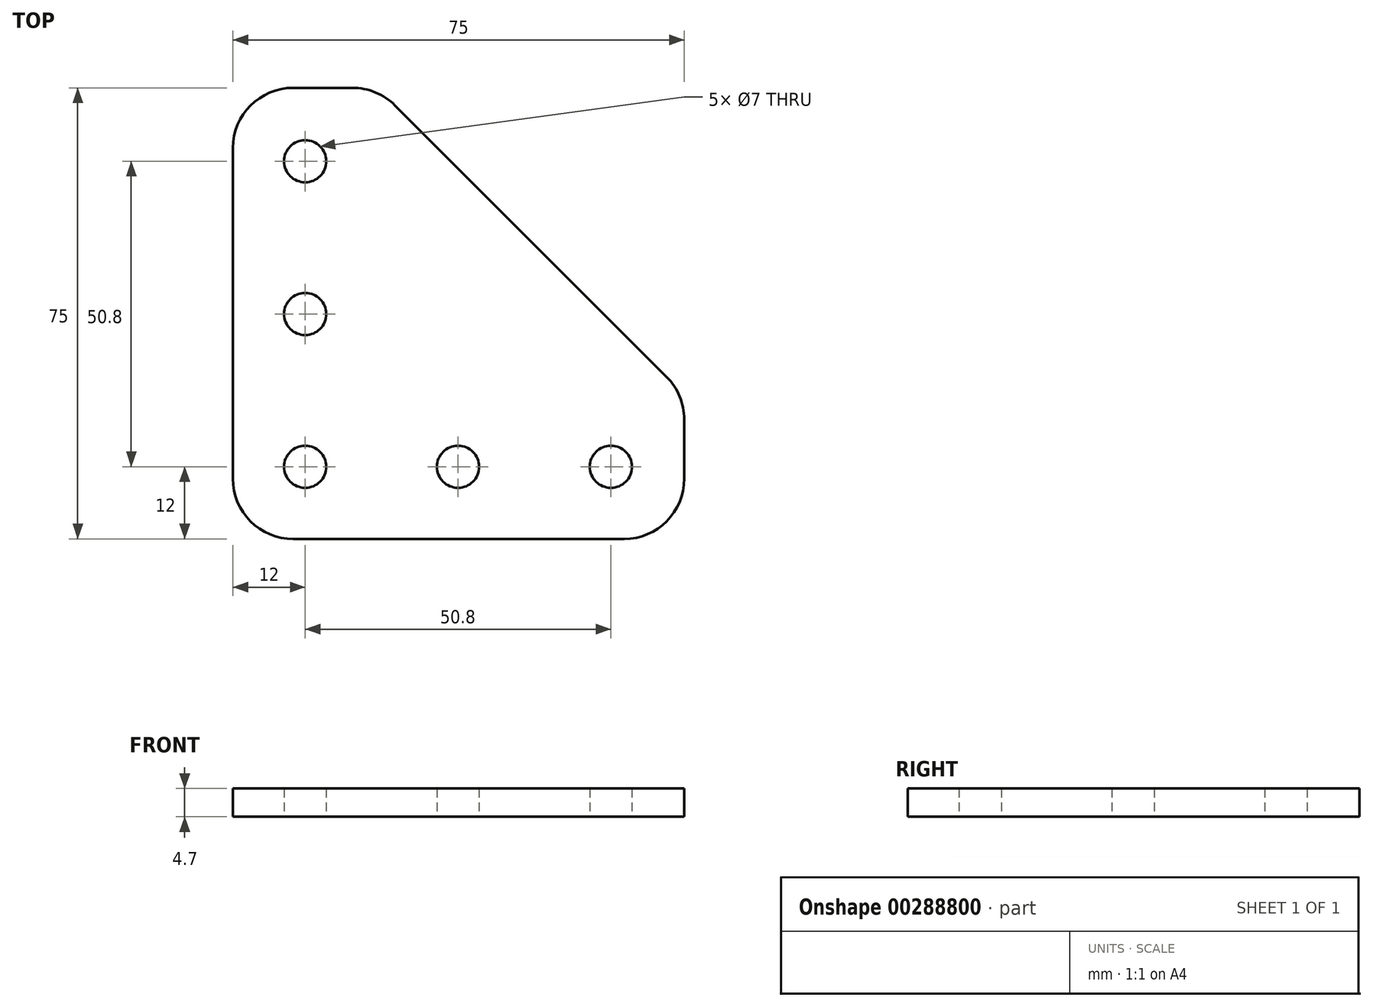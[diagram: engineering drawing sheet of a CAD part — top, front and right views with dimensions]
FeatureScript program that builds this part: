
annotation { "Feature Type Name" : "Feature", "Feature Type Description" : "" }
export const myFeature = defineFeature(function(context is Context, id is Id, definition is map)
    precondition{}
    {
        {
            var Q0;
            Q0=qCreatedBy(makeId("Top.planeOp"),FACE);
            var sketch = newSketch(context, id + "F0", { "sketchPlane" : qUnion([Q0])});
            skLineSegment(sketch, "E0", {"start": v(0, 0) * mm, "end": v(75, 0) * mm});
            skLineSegment(sketch, "E1", {"start": v(75, 0) * mm, "end": v(75, 24) * mm});
            skLineSegment(sketch, "E2", {"start": v(75, 24) * mm, "end": v(24, 75) * mm});
            skLineSegment(sketch, "E3", {"start": v(24, 75) * mm, "end": v(0, 75) * mm});
            skLineSegment(sketch, "E4", {"start": v(0, 75) * mm, "end": v(0, 0) * mm});
            skCircle(sketch, "E5", {"center": v(12, 37.4) * mm, "radius": 3.5 * mm});
            skCircle(sketch, "E6", {"center": v(12, 12) * mm, "radius": 3.5 * mm});
            skCircle(sketch, "E7", {"center": v(37.4, 12) * mm, "radius": 3.5 * mm});
            skLineSegment(sketch, "E8", {"start": v(37.4, 12) * mm, "end": v(12, 12) * mm, "construction": true});
            skLineSegment(sketch, "E9", {"start": v(12, 37.4) * mm, "end": v(12, 12) * mm, "construction": true});
            skLineSegment(sketch, "E10", {"start": v(37.4, 12) * mm, "end": v(75, 12) * mm, "construction": true});
            skLineSegment(sketch, "E11", {"start": v(12, 37.4) * mm, "end": v(12, 75) * mm, "construction": true});
            skCircle(sketch, "E12", {"center": v(12, 62.8) * mm, "radius": 3.5 * mm});
            skCircle(sketch, "E13", {"center": v(62.8, 12) * mm, "radius": 3.5 * mm});
            skSolve(sketch);
        }
        {
            var Q0;
            Q0=makeQuery(id+"F0.imprint","IMPRINT",FACE,{"disambiguationData":[TD([[makeQuery(id+"F0.imprint","IMPRINT",EDGE,{"derivedFrom":sQuery(id+"F0.wireOp",EDGE,"E0")}),1.0]])]});
            extrude(context, id + "F1", {"entities" : qUnion([Q0]), "depth" : 4.7 * mm});
        }
        {
            var Q0;
            Q0=makeQuery(id+"F1.opExtrude","SWEPT_EDGE",EDGE,{"disambiguationData":[OSD([sQuery(id+"F0.wireOp",EDGE,"E0"),sQuery(id+"F0.wireOp",EDGE,"E1")])]});
            var Q1;
            Q1=makeQuery(id+"F1.opExtrude","SWEPT_EDGE",EDGE,{"disambiguationData":[OSD([sQuery(id+"F0.wireOp",EDGE,"E0"),sQuery(id+"F0.wireOp",EDGE,"E4")])]});
            var Q2;
            Q2=makeQuery(id+"F1.opExtrude","SWEPT_EDGE",EDGE,{"disambiguationData":[OSD([sQuery(id+"F0.wireOp",EDGE,"E1"),sQuery(id+"F0.wireOp",EDGE,"E2")])]});
            var Q3;
            Q3=makeQuery(id+"F1.opExtrude","SWEPT_EDGE",EDGE,{"disambiguationData":[OSD([sQuery(id+"F0.wireOp",EDGE,"E2"),sQuery(id+"F0.wireOp",EDGE,"E3")])]});
            var Q4;
            Q4=makeQuery(id+"F1.opExtrude","SWEPT_EDGE",EDGE,{"disambiguationData":[OSD([sQuery(id+"F0.wireOp",EDGE,"E3"),sQuery(id+"F0.wireOp",EDGE,"E4")])]});
            fillet(context, id + "F2", {"entities" : qUnion([Q0, Q1, Q2, Q3, Q4]), "radius" : 10 * mm, "tangentPropagation" : true, "allowEdgeOverflow" : false});
        }
    });
